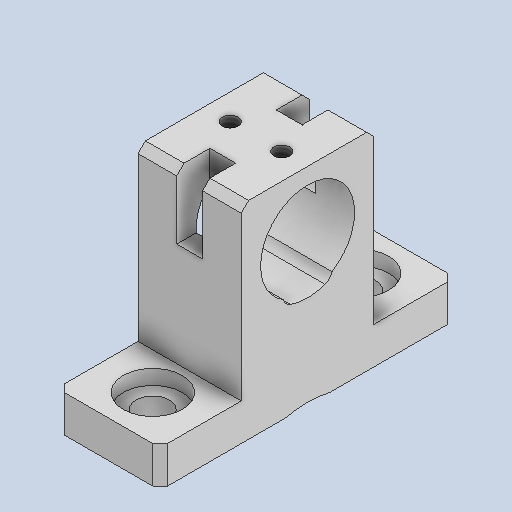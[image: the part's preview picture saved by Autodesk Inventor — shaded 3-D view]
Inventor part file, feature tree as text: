
AUTODESK INVENTOR PART (.ipt)
format: ipt  version: 2024.2 (Build 282272000, 272)  size: 310,784 bytes
history: native  units: in
note: dims shown in document units (in); Inventor stores cm internally (conversion verified against a paired STEP export)
features: extrude x6, other x5, hole x3, chamfer x2, sketch x1
ambient origin geometry x8: Origin, YZ Plane, XZ Plane, XY Plane, X Axis, Y Axis, Z Axis, Center Point
bodies: Solid1 (feature_tree)
feature tree (17):
  other  "Table"
  other  "ADAPTER_collimator-BH32-D12.7"
  other  "ADAPTER_collimator-BH12.7-D12.7"
  other  "ADAPTER_collimator-BH19.05-D12.7"
  other  "ADAPTER_collimator-BH32-60FC-SF"
  extrude  "Extrusion1"  TaperAngle=0.0deg  [1 undecoded]
  extrude  "Extrusion2"  Depth=0.4331in
  hole  "Hole1"  [1 undecoded]
  chamfer  "Chamfer2"  [1 undecoded]
  extrude  "Extrusion6"  Depth=0.75in
  hole  "Hole3"  [1 undecoded]
  chamfer  "Chamfer3"  Distance=0.12in
  extrude  "Extrusion7"  Depth=0.75in
  hole  "Hole4"  [1 undecoded]
  extrude  "Extrusion8"  Depth=0.75in
  extrude  "Extrusion9"  Depth=0.1378in
  sketch  "Sketch10"  dims[d3=0.0in d4=0.0in d5=0.4331in d6=0.1969in d7=0.0in d8=0.1772in d9=0.2362in d10=0.315in d11=0.0787in d12=0.5635in d13=0.315in d14=0.8108in d15=0.0in d16=0.2362in d35=0.0394in d36=0.0787in d37=45.0deg d51=0.12in d52=0.1374in d53=0.0in d54=0.0in d55=0.3543in d57=0.0849in d58=0.224in d59=0.2188in d60=0.112in d61=0.5635in d62=0.349in d63=0.0in d64=0.1378in d65=0.3543in d66=0.0394in d67=0.0787in d68=45.0deg d69=0.3543in d70=0.0in d71=0.1772in d72=0.1378in d73=0.0689in d74=0.3937in d75=0.0in d76=0.0in d77=0.1969in d78=0.0413in d79=0.0394in d80=0.0827in d81=0.2362in d82=0.3126in d83=0.1642in d84=0.5635in d85=0.0827in d86=0.0in d87=0.0827in d88=0.0in d89=0.0in d90=0.4862in d91=1.0in d92=0.1969in d93=0.0in d94=0.1378in d95=0.4724in d96=0.75in d17=0.0197in d18=0.0344in d19=0.0197in d20=0.0344in]
note: 5 required parameter values undecoded (feature->parameter linkage not recoverable at this tier; creation-order binding heuristic only, values carry confidence <= 0.55)
